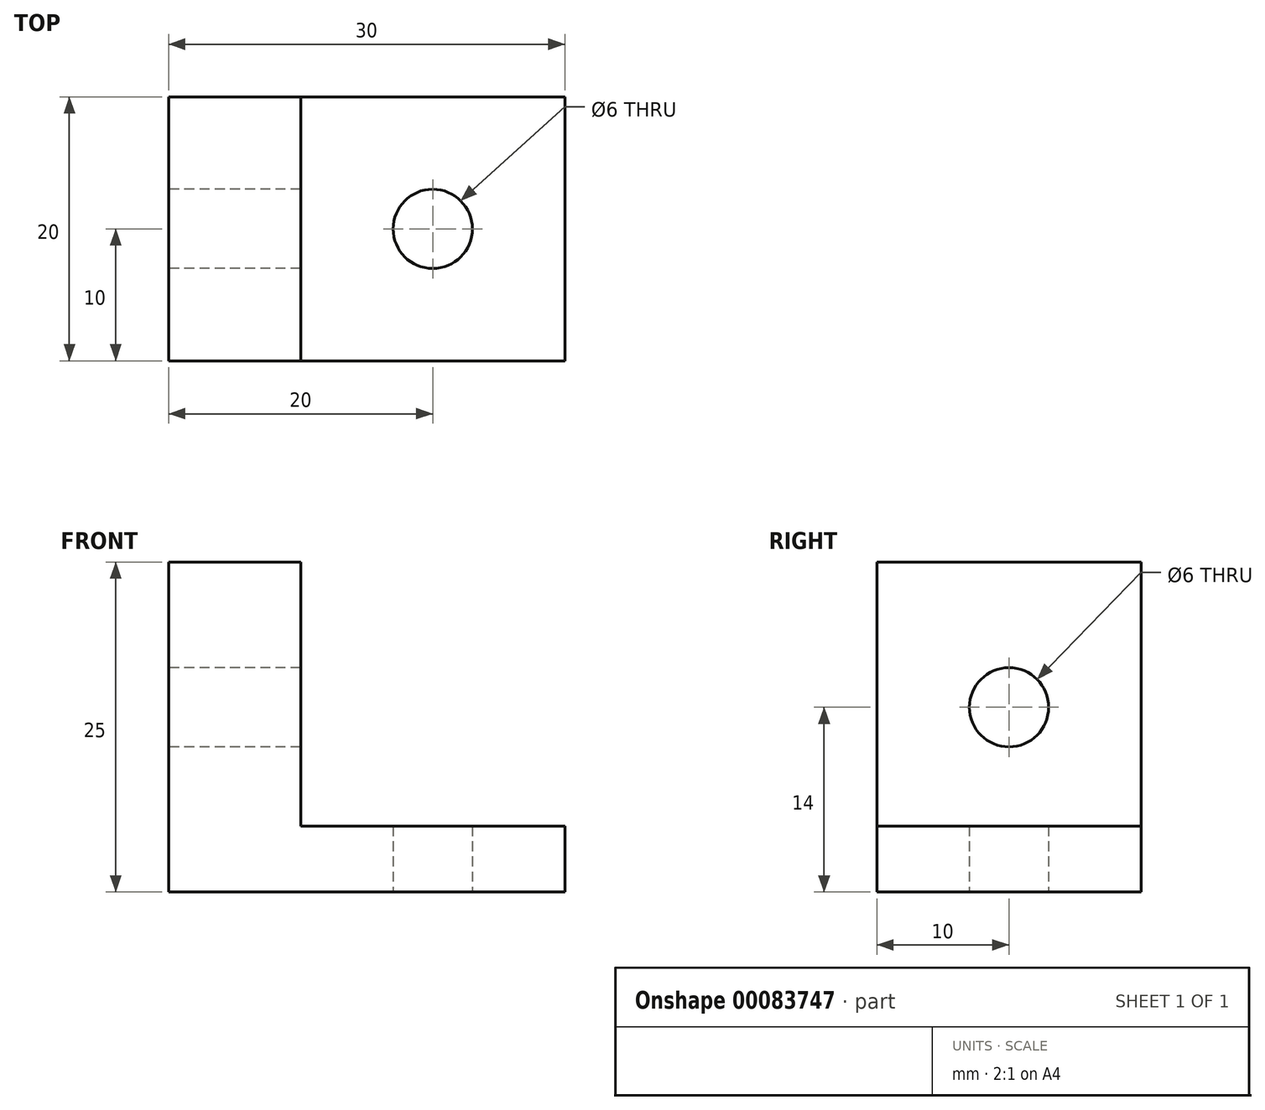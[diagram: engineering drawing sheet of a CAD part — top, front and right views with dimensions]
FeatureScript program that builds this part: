
annotation { "Feature Type Name" : "Feature", "Feature Type Description" : "" }
export const myFeature = defineFeature(function(context is Context, id is Id, definition is map)
    precondition{}
    {
        {
            var Q0;
            Q0=qCreatedBy(makeId("Top.planeOp"),FACE);
            var sketch = newSketch(context, id + "F0", { "sketchPlane" : qUnion([Q0])});
            skLineSegment(sketch, "E0.bottom", {"start": v(0, 0) * mm, "end": v(30, 0) * mm});
            skLineSegment(sketch, "E0.top", {"start": v(0, 20) * mm, "end": v(30, 20) * mm});
            skLineSegment(sketch, "E0.left", {"start": v(0, 0) * mm, "end": v(0, 20) * mm});
            skLineSegment(sketch, "E0.right", {"start": v(30, 0) * mm, "end": v(30, 20) * mm});
            skLineSegment(sketch, "E1", {"start": v(10, 20) * mm, "end": v(10, 0) * mm});
            skCircle(sketch, "E2", {"center": v(20, 10) * mm, "radius": 3 * mm});
            skSolve(sketch);
        }
        {
            var Q0;
            {var subQ4=sQuery(id+"F0.wireOp",EDGE,"E0.right");Q0=makeQuery(id+"F0.imprint","IMPRINT",FACE,{"disambiguationData":[TD([[makeQuery(id+"F0.imprint","IMPRINT",EDGE,{"derivedFrom":subQ4}),1.0]])]});}
            var Q1;
            {var subQ5=sQuery(id+"F0.wireOp",EDGE,"dWPc2AZj-42NN-oB4P-onDy-kEAOytmciOfd");Q1=makeQuery(id+"F0.imprint","IMPRINT",FACE,{"disambiguationData":[TD([[makeQuery(id+"F0.imprint","IMPRINT",EDGE,{"derivedFrom":subQ5}),1.0]])]});}
            var Q2;
            {var subQ5=sQuery(id+"F0.wireOp",EDGE,"Q3B7iM1n-GUiq-EYFl-fATP-MUHIS3hWslFc");Q2=makeQuery(id+"F0.imprint","IMPRINT",FACE,{"disambiguationData":[TD([[makeQuery(id+"F0.imprint","IMPRINT",EDGE,{"derivedFrom":subQ5}),-1.0]])]});}
            var Q3;
            {var subQ0=sQuery(id+"F0.wireOp",EDGE,"dWPc2AZj-42NN-oB4P-onDy-kEAOytmciOfd");Q3=makeQuery(id+"F0.imprint","IMPRINT",FACE,{"disambiguationData":[TD([[makeQuery(id+"F0.imprint","IMPRINT",EDGE,{"derivedFrom":subQ0}),-1.0]])]});}
            extrude(context, id + "F1", {"entities" : qUnion([Q0, Q1, Q2, Q3]), "depth" : 5 * mm});
        }
        {
            var Q0;
            {var subQ0=sQuery(id+"F0.wireOp",EDGE,"E0.left");Q0=makeQuery(id+"F0.imprint","IMPRINT",FACE,{"disambiguationData":[TD([[makeQuery(id+"F0.imprint","IMPRINT",EDGE,{"derivedFrom":subQ0}),-1.0]])]});}
            extrude(context, id + "F2", {"entities" : qUnion([Q0]), "operationType" : NewBodyOperationType.ADD, "depth" : 25 * mm});
        }
        {
            var Q0;
            Q0=qCreatedBy(makeId("Right.planeOp"),FACE);
            var sketch = newSketch(context, id + "F3", { "sketchPlane" : qUnion([Q0])});
            skCircle(sketch, "E3", {"center": v(10, 14) * mm, "radius": 3 * mm});
            skSolve(sketch);
        }
        {
            var Q0;
            Q0=makeQuery(id+"F3.imprint","IMPRINT",FACE,{"disambiguationData":[TD([[makeQuery(id+"F3.imprint","IMPRINT",EDGE,{"derivedFrom":sQuery(id+"F3.wireOp",EDGE,"E3")}),1.0]])]});
            extrude(context, id + "F4", {"entities" : qUnion([Q0]), "operationType" : NewBodyOperationType.REMOVE, "depth" : 25 * mm});
        }
    });
